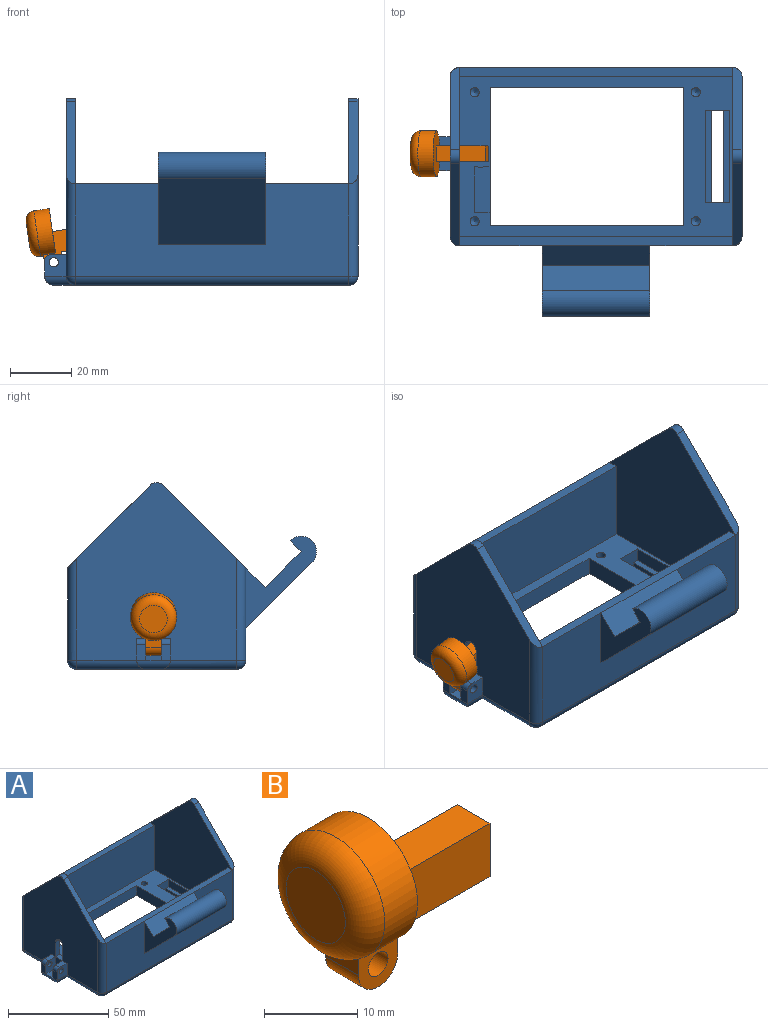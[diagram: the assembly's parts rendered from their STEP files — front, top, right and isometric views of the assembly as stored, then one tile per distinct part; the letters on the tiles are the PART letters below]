
ASSEMBLY  parts=2 mates=1
PART A: 85 faces, bbox 102x81x60.8 mm
  f0: plane 5x3mm, normal (-1,0,0), area 15mm2, adj f45,f47,f53,f79
  f1: plane 89x3mm, normal (0,0,1), area 267mm2, adj f6,f11,f38,f39,f56
  f2: plane 89x3mm, normal (0,0,1), area 267mm2, adj f6,f13,f38,f40
  f3: plane 7x7mm, normal (0,1,0), area 41.1mm2, adj f4,f48,f49,f51,f54,f55
  f4: plane 7x5mm, normal (-1,0,0), area 35mm2, adj f3,f44,f45,f55
  f5: plane 57.76x52mm, normal (-1,0,0), area 2258.3mm2, adj f41,f42,f43,f46,f47,f49,f50,f65
  f6: plane 58x54.76mm, normal (1,0,0), area 2188.3mm2, adj f1,f2,f7,f39,f40,f41,f42,f43
  f7: plane 89x52mm, normal (0,0,1), area 1454.5mm2, adj f6,f8,f9,f10,f15,f17,f18,f20
  f8: plane 63x6mm, normal (0,1,0), area 378mm2, adj f7,f9,f18,f19
  f9: plane 45x6mm, normal (1,0,0), area 203.9mm2, adj f7,f8,f10,f19,f24,f28,f29
  f10: plane 63x6mm, normal (0,-1,0), area 378mm2, adj f7,f9,f18,f19
  f11: plane 89x30mm, normal (0,-1,0), area 1977.6mm2, adj f1,f60,f61,f62,f69,f70,f71
  f12: plane 57.76x52mm, normal (1,0,0), area 2390.1mm2, adj f63,f64,f68,f71,f75,f76
  f13: plane 89x30mm, normal (0,1,0), area 2670mm2, adj f2,f76,f80,f81
  f14: plane 30x1.5mm, normal (-1,0,0), area 45mm2, adj f15,f17,f19,f23
  f15: plane 7.9x6mm, normal (0,1,0), area 41.4mm2, adj f7,f14,f16,f19,f20,f21,f22,f23
  f16: plane 30x1.5mm, normal (1,0,0), area 45mm2, adj f15,f17,f19,f21
  f17: plane 7.9x6mm, normal (0,-1,0), area 41.4mm2, adj f7,f14,f16,f19,f20,f21,f22,f23
  f18: plane 45x6mm, normal (-1,0,0), area 270mm2, adj f7,f8,f10,f19
  f19: plane 96x52mm, normal (0,0,-1), area 1711mm2, adj f8,f9,f10,f14,f15,f16,f17,f18
  f20: plane 30x4.5mm, normal (1,0,0), area 135mm2, adj f7,f15,f17,f21
  f21: plane 30x2mm, normal (0,0,1), area 60mm2, adj f15,f16,f17,f20
  f22: plane 30x4.5mm, normal (-1,0,0), area 135mm2, adj f7,f15,f17,f23
  f23: plane 30x2mm, normal (0,0,1), area 60mm2, adj f14,f15,f17,f22
  f24: plane 4.5x2.05mm, normal (0,-1,0), area 9.2mm2, adj f7,f9,f25,f29
  f25: cylinder r=2.5mm len=4.5mm, axis (0,0,1), area 8.8mm2, adj f7,f24,f26,f29
  f26: plane 4.5x1.05mm, normal (0,-1,0), area 4.7mm2, adj f7,f25,f27,f29
  f27: plane 14.69x4.5mm, normal (1,0,0), area 66.1mm2, adj f7,f26,f28,f29
  f28: plane 5x4.5mm, normal (0,1,0), area 22.5mm2, adj f7,f9,f27,f29
  f29: plane 14.69x5mm, normal (0,0,1), area 73.2mm2, adj f9,f24,f25,f26,f27,f28
  f30: cone r=0mm half-angle=59deg, axis (0,0,1), area 8.2mm2, adj f31
  f31: cylinder r=1.5mm len=4mm, axis (0,0,1), area 37.7mm2, adj f7,f30
  f32: cone r=0mm half-angle=59deg, axis (0,0,1), area 8.2mm2, adj f33
  f33: cylinder r=1.5mm len=4mm, axis (0,0,1), area 37.7mm2, adj f7,f32
  f34: cone r=0mm half-angle=59deg, axis (0,0,1), area 8.2mm2, adj f35
  f35: cylinder r=1.5mm len=4mm, axis (0,0,1), area 37.7mm2, adj f7,f34
  f36: cone r=0mm half-angle=59deg, axis (0,0,1), area 8.2mm2, adj f37
  f37: cylinder r=1.5mm len=4mm, axis (0,0,1), area 37.7mm2, adj f7,f36
  f38: plane 58x54.76mm, normal (-1,0,0), area 2243.1mm2, adj f1,f2,f7,f39,f40,f63,f64,f68
  f39: plane 89x27mm, normal (0,1,0), area 2403mm2, adj f1,f6,f7,f38
  f40: plane 89x27mm, normal (0,-1,0), area 2403mm2, adj f2,f6,f7,f38
  f41: plane 9x3mm, normal (0,-1,0), area 27mm2, adj f5,f6,f42,f44
  f42: cylinder r=2.5mm len=5mm, axis (1,0,0), area 23.6mm2, adj f5,f6,f41,f43
  f43: plane 9x3mm, normal (0,1,0), area 27mm2, adj f5,f6,f42,f44
  f44: plane 5x3mm, normal (0,0,1), area 15mm2, adj f4,f6,f41,f43
  f45: plane 7x7mm, normal (0,-1,0), area 41.1mm2, adj f0,f4,f46,f52,f53,f55
  f46: plane 5x3mm, normal (0,0,1), area 15mm2, adj f5,f45,f47,f53
  f47: plane 7x7mm, normal (0,1,0), area 41.1mm2, adj f0,f5,f46,f52,f53,f82
  f48: plane 5x3mm, normal (-1,0,0), area 15mm2, adj f3,f50,f54,f79
  f49: plane 5x3mm, normal (0,0,1), area 15mm2, adj f3,f5,f50,f54
  f50: plane 7x7mm, normal (0,-1,0), area 41.1mm2, adj f5,f48,f49,f51,f54,f77
  f51: cylinder r=1.5mm len=3mm, axis (0,1,0), area 28.3mm2, adj f3,f50
  f52: cylinder r=1.5mm len=3mm, axis (0,1,0), area 28.3mm2, adj f45,f47
  f53: cylinder r=2mm len=3mm, axis (0,-1,0), area 9.4mm2, adj f0,f45,f46,f47
  f54: cylinder r=2mm len=3mm, axis (0,-1,0), area 9.4mm2, adj f3,f48,f49,f50
  f55: plane 7x5mm, normal (0,0,1), area 35mm2, adj f3,f4,f45,f79
  f56: plane 35x6.36mm, normal (0,-0.71,0.71), area 314.6mm2, adj f1,f57,f61,f62
  f57: plane 35x11.67mm, normal (0,0.71,0.71), area 577.5mm2, adj f56,f58,f61,f62
  f58: plane 35x3.54mm, normal (0,0.71,-0.71), area 175mm2, adj f57,f59,f61,f62
  f59: cylinder r=5mm len=35mm, axis (1,0,0), area 549.8mm2, adj f58,f60,f61,f62
  f60: plane 35x21.56mm, normal (0,-0.71,-0.71), area 1067.1mm2, adj f11,f59,f61,f62
  f61: plane 30.09x23.02mm, normal (-1,0,0), area 219.6mm2, adj f11,f56,f57,f58,f59,f60
  f62: plane 30.09x23.02mm, normal (1,0,0), area 219.6mm2, adj f11,f56,f57,f58,f59,f60
  f63: plane 26.88x26.88mm, normal (0,0.71,0.71), area 111.3mm2, adj f12,f38,f68,f76
  f64: plane 26.88x26.88mm, normal (0,-0.71,0.71), area 111.3mm2, adj f12,f38,f68,f71
  f65: plane 26.88x26.88mm, normal (0,0.71,0.71), area 111.3mm2, adj f5,f6,f67,f81
  f66: plane 26.88x26.88mm, normal (0,-0.71,0.71), area 111.3mm2, adj f5,f6,f67,f69
  f67: cylinder r=3mm len=4.24mm, axis (-1,0,0), area 14.1mm2, adj f5,f6,f65,f66
  f68: cylinder r=3mm len=4.24mm, axis (-1,0,0), area 14.1mm2, adj f12,f38,f63,f64
  f69: cylinder r=3mm len=33mm, axis (0,0,-1), area 146.5mm2, adj f5,f11,f66,f72
  f70: cylinder r=3mm len=89mm, axis (-1,0,0), area 419.4mm2, adj f11,f19,f72,f73
  f71: cylinder r=3mm len=33mm, axis (0,0,1), area 146.5mm2, adj f11,f12,f64,f73
  f72: sphere r=3mm, area 14.1mm2, adj f69,f70,f74
  f73: sphere r=3mm, area 14.1mm2, adj f70,f71,f75
  f74: cylinder r=3mm len=24.5mm, axis (0,1,0), area 106.5mm2, adj f5,f19,f72,f77
  f75: cylinder r=3mm len=52mm, axis (0,-1,0), area 245mm2, adj f12,f19,f73,f78
  f76: cylinder r=3mm len=33mm, axis (0,0,-1), area 146.5mm2, adj f12,f13,f63,f78
  f77: cylinder r=3mm len=10mm, axis (-1,0,0), area 33mm2, adj f19,f50,f74,f79
  f78: sphere r=3mm, area 14.1mm2, adj f75,f76,f80
  f79: cylinder r=3mm len=11mm, axis (0,-1,0), area 41.6mm2, adj f0,f19,f48,f55,f77,f82
  f80: cylinder r=3mm len=89mm, axis (1,0,0), area 419.4mm2, adj f13,f19,f78,f83
  f81: cylinder r=3mm len=33mm, axis (0,0,1), area 146.5mm2, adj f5,f13,f65,f83
  f82: cylinder r=3mm len=10mm, axis (1,0,0), area 33mm2, adj f19,f47,f79,f84
  f83: sphere r=3mm, area 14.1mm2, adj f80,f81,f84
  f84: cylinder r=3mm len=22.5mm, axis (0,1,0), area 97mm2, adj f5,f19,f82,f83
PART B: 13 faces, bbox 24x16.2x21.1 mm
  f0: plane 20x13mm, normal (0,1,0), area 136.8mm2, adj f1,f3,f4,f5,f6,f7,f8,f9
  f1: plane 16x5mm, normal (0,0,1), area 80mm2, adj f0,f2,f8,f10
  f2: plane 20x13mm, normal (0,-1,0), area 136.8mm2, adj f1,f3,f4,f5,f6,f7,f8,f9
  f3: cylinder r=3mm len=6mm, axis (0,-1,0), area 47.1mm2, adj f0,f2,f4,f5
  f4: plane 5x2.93mm, normal (-1,0,0), area 13.2mm2, adj f0,f2,f3,f9
  f5: plane 5x3mm, normal (1,0,0), area 15mm2, adj f0,f2,f3,f7
  f6: cylinder r=1.5mm len=5mm, axis (0,-1,0), area 47.1mm2, adj f0,f2
  f7: plane 14x5mm, normal (0,0,-1), area 70mm2, adj f0,f2,f5,f8
  f8: plane 7x5mm, normal (1,0,0), area 35mm2, adj f0,f1,f2,f7
  f9: cylinder r=7.5mm len=15mm, axis (1,0,0), area 215.2mm2, adj f0,f2,f4,f10,f12
  f10: plane 15x14.57mm, normal (1,0,0), area 139.9mm2, adj f0,f1,f2,f9
  f11: plane 9x9mm, normal (-1,0,0), area 63.6mm2, adj f12
  f12: torus R=4.5mm, axis (-1,0,0), area 189.8mm2, adj f9,f11
PLACE A t=(-13.36,5.62,-0.14)mm fixed
PLACE B rot(axis=(0,-1,0),8.3deg) t=(-13.66,5.62,6.96)mm
MATE revolute A.f51 <-> B.f3  axis (0,1,0) through (-62.57,3.76,1.36)mm
